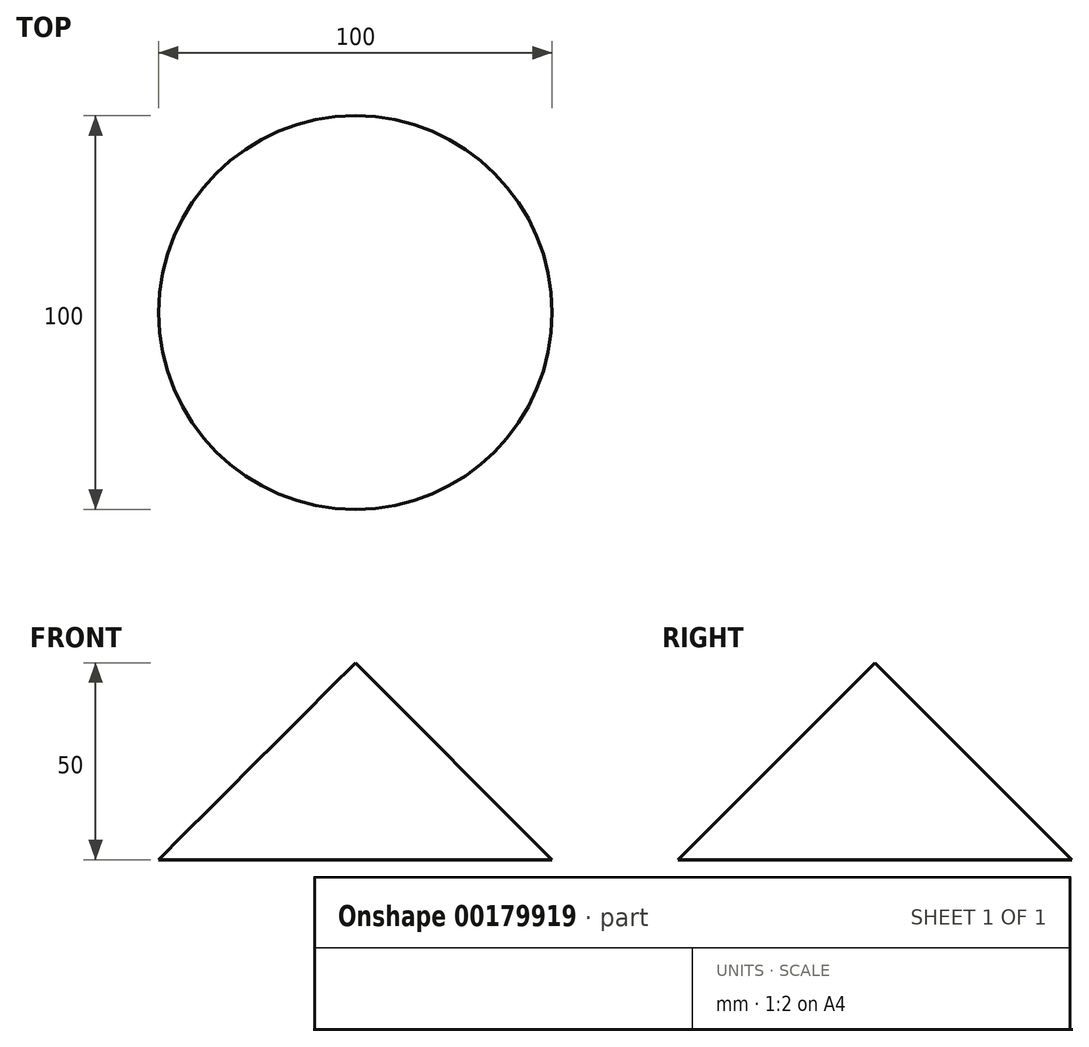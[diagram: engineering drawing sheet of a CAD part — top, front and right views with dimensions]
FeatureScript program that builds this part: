
annotation { "Feature Type Name" : "Feature", "Feature Type Description" : "" }
export const myFeature = defineFeature(function(context is Context, id is Id, definition is map)
    precondition{}
    {
        {
            var Q0;
            Q0=qCreatedBy(makeId("Front.planeOp"),FACE);
            var sketch = newSketch(context, id + "F0", { "sketchPlane" : qUnion([Q0])});
            skLineSegment(sketch, "E0", {"start": v(0, 0) * mm, "end": v(50, 0) * mm});
            skLineSegment(sketch, "E1", {"start": v(50, 0) * mm, "end": v(0, 50) * mm});
            skLineSegment(sketch, "E2", {"start": v(0, 50) * mm, "end": v(0, 0) * mm});
            skSolve(sketch);
        }
        {
            var Q0;
            Q0=makeQuery(id+"F0.imprint","IMPRINT",FACE,{"disambiguationData":[TD([[makeQuery(id+"F0.imprint","IMPRINT",EDGE,{"derivedFrom":sQuery(id+"F0.wireOp",EDGE,"E0")}),1.0]])]});
            var Q1;
            Q1=sQuery(id+"F0.wireOp",EDGE,"E2");
            revolve(context, id + "F1", {"entities" : qUnion([Q0]), "axis" : qUnion([Q1]), "revolveType" : RevolveType.FULL});
        }
    });
